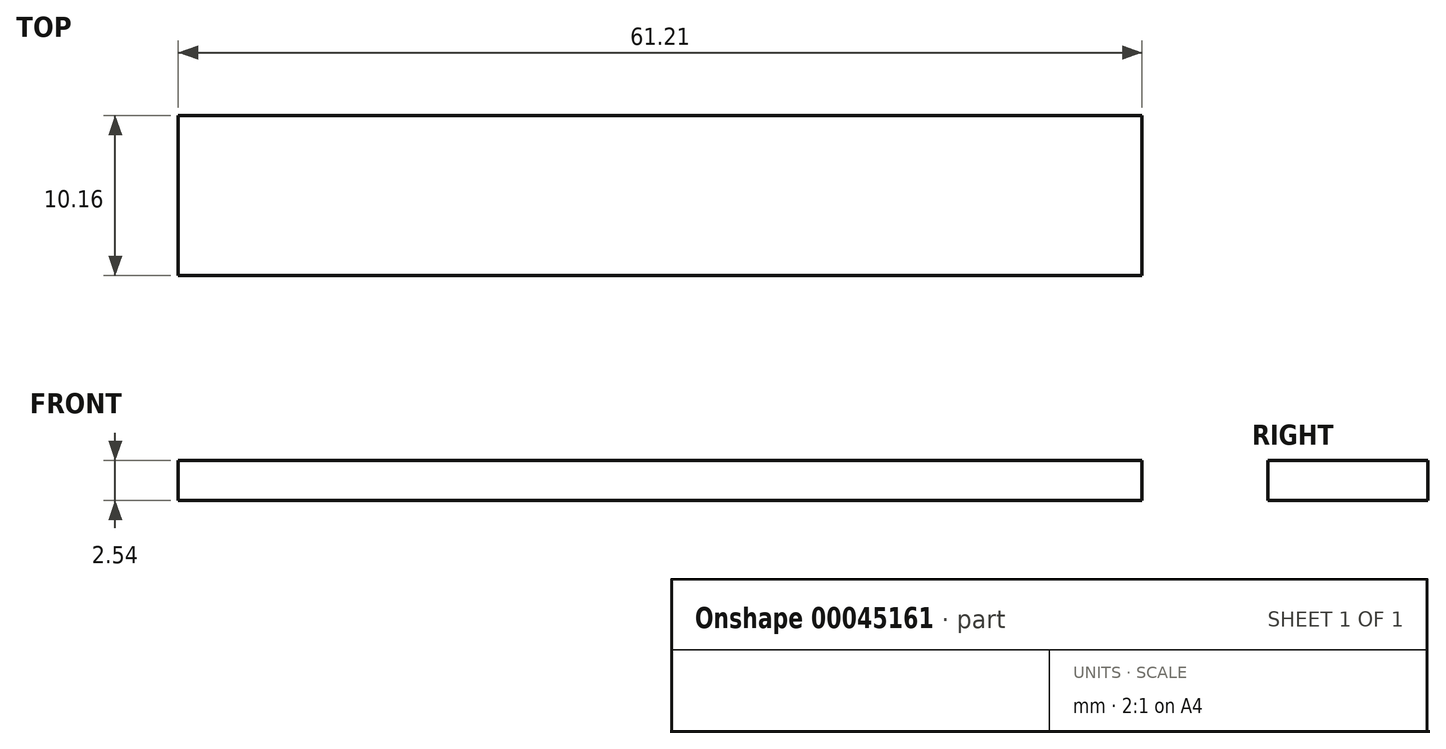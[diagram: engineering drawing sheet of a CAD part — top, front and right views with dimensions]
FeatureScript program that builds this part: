
annotation { "Feature Type Name" : "Feature", "Feature Type Description" : "" }
export const myFeature = defineFeature(function(context is Context, id is Id, definition is map)
    precondition{}
    {
        {
            var Q0;
            Q0=qCreatedBy(makeId("Front.planeOp"),FACE);
            var sketch = newSketch(context, id + "F0", { "sketchPlane" : qUnion([Q0])});
            skLineSegment(sketch, "E0", {"start": v(0, 0) * mm, "end": v(61.21, 0) * mm});
            skLineSegment(sketch, "E1", {"start": v(61.21, 0) * mm, "end": v(61.21, 2.54) * mm});
            skLineSegment(sketch, "E2", {"start": v(61.21, 2.54) * mm, "end": v(0, 2.54) * mm});
            skLineSegment(sketch, "E3", {"start": v(0, 2.54) * mm, "end": v(0, 0) * mm});
            skSolve(sketch);
        }
        {
            var Q0;
            Q0 = qSketchRegion(id + "F0", true);
            extrude(context, id + "F1", {"entities" : qUnion([Q0]), "depth" : 10.16 * mm});
        }
    });
